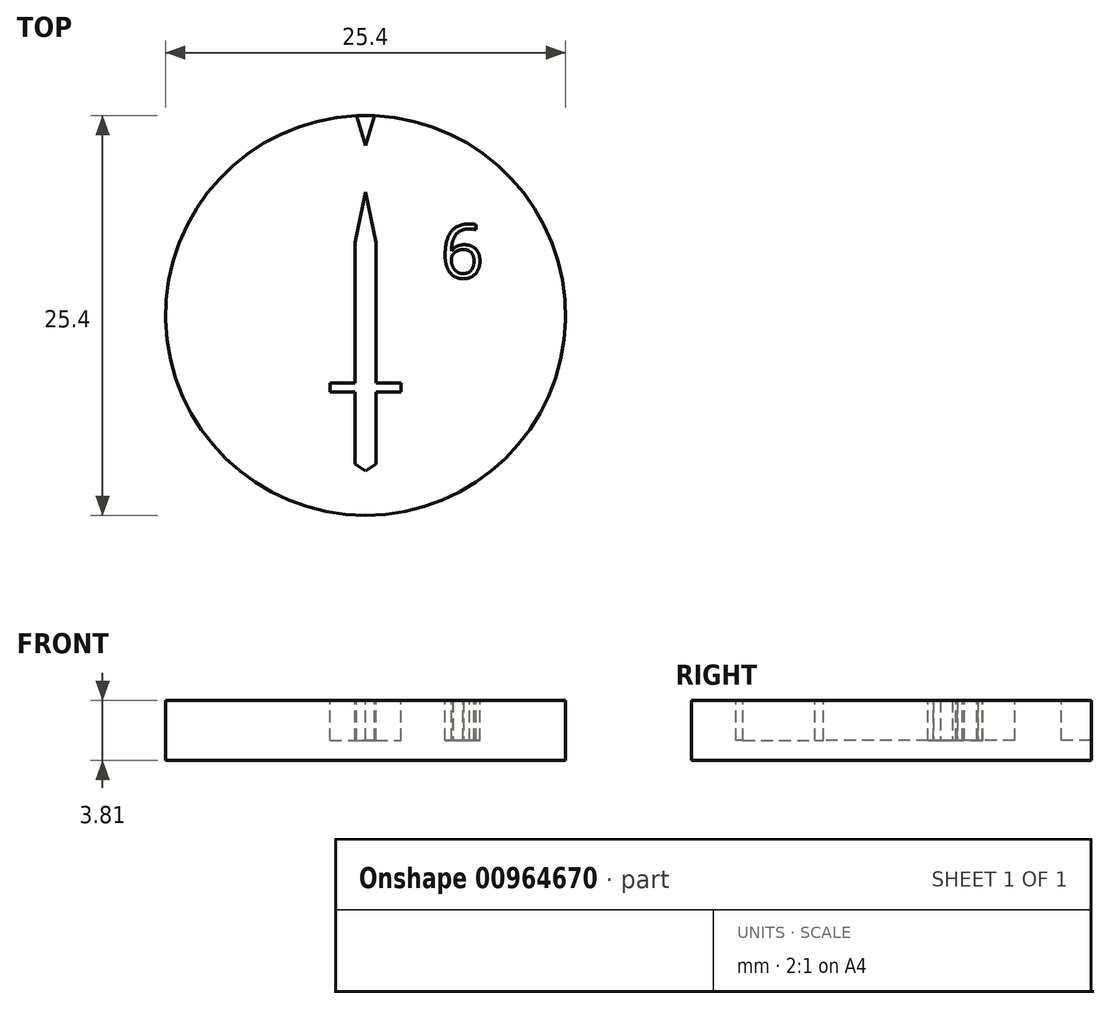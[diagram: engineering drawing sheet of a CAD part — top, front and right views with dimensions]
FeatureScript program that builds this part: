
annotation { "Feature Type Name" : "Feature", "Feature Type Description" : "" }
export const myFeature = defineFeature(function(context is Context, id is Id, definition is map)
    precondition{}
    {
        {
            var Q0;
            Q0=qCreatedBy(makeId("Top.planeOp"),FACE);
            var sketch = newSketch(context, id + "F0", { "sketchPlane" : qUnion([Q0])});
            skCircle(sketch, "E0", {"center": v(0, 0) * mm, "radius": 12.7 * mm});
            skSolve(sketch);
        }
        {
            var Q0;
            Q0=makeQuery(id+"F0.imprint","IMPRINT",FACE,{"disambiguationData":[TD([[makeQuery(id+"F0.imprint","IMPRINT",EDGE,{"derivedFrom":sQuery(id+"F0.wireOp",EDGE,"E0")}),1.0]])]});
            extrude(context, id + "F1", {"entities" : qUnion([Q0]), "depth" : 3.8 * mm, "offsetDistance" : 25.4 * mm});
        }
        {
            var Q0;
            Q0=makeQuery(id+"F1.opExtrude","CAP_FACE",FACE,{"disambiguationData":[OSD([sQuery(id+"F0.wireOp",EDGE,"E0")])],"isStart":false});
            var sketch = newSketch(context, id + "F2", { "sketchPlane" : qUnion([Q0])});
            skLineSegment(sketch, "E1", {"start": v(-0.56, 12.69) * mm, "end": v(0, 10.8) * mm});
            skLineSegment(sketch, "E2", {"start": v(0, 10.8) * mm, "end": v(0.56, 12.69) * mm});
            skLineSegment(sketch, "E3", {"start": v(2.27, -4.3) * mm, "end": v(0.66, -4.3) * mm});
            skLineSegment(sketch, "E4", {"start": v(2.27, -4.3) * mm, "end": v(2.27, -4.86) * mm});
            skLineSegment(sketch, "E5", {"start": v(0.66, -4.86) * mm, "end": v(2.27, -4.86) * mm});
            skLineSegment(sketch, "E6", {"start": v(0.66, -4.86) * mm, "end": v(0.66, -9.43) * mm});
            skLineSegment(sketch, "E7", {"start": v(-0.66, -9.43) * mm, "end": v(-0.66, -4.86) * mm});
            skLineSegment(sketch, "E8", {"start": v(-2.27, -4.86) * mm, "end": v(-0.66, -4.86) * mm});
            skLineSegment(sketch, "E9", {"start": v(-2.27, -4.86) * mm, "end": v(-2.27, -4.3) * mm});
            skLineSegment(sketch, "E10", {"start": v(-0.66, -4.3) * mm, "end": v(-2.27, -4.3) * mm});
            skLineSegment(sketch, "E11", {"start": v(-0.66, -4.3) * mm, "end": v(-0.66, 4.63) * mm});
            skLineSegment(sketch, "E12", {"start": v(-0.66, 4.63) * mm, "end": v(0, 7.84) * mm});
            skLineSegment(sketch, "E13", {"start": v(0, 7.84) * mm, "end": v(0.66, 4.63) * mm});
            skLineSegment(sketch, "E14", {"start": v(0.66, 4.63) * mm, "end": v(0.66, -4.3) * mm});
            skLineSegment(sketch, "E15", {"start": v(-0.66, -9.43) * mm, "end": v(0, -9.88) * mm});
            skLineSegment(sketch, "E16", {"start": v(0, -9.88) * mm, "end": v(0.66, -9.43) * mm});
            skText(sketch, "E17", { "text": "6", "fontName": "OpenSans-Regular.ttf"});
            const initialGuessF2  = {"E17": [0.00478, 0.00238, 1, 0, 0.00342]};
            skSetInitialGuess(sketch, initialGuessF2);
            skSolve(sketch);
        }
        {
            var Q0;
            Q0 = qSketchRegion(id + "F2", true);
            var Q1;
            {var subQ0=sQuery(id+"F2.wireOp",EDGE,"E1");Q1=makeQuery(id+"F2.imprint","IMPRINT",FACE,{"disambiguationData":[TD([[makeQuery(id+"F2.imprint","IMPRINT",EDGE,{"derivedFrom":subQ0}),1.0]])]});}
            extrude(context, id + "F3", {"entities" : qUnion([Q0, Q1]), "operationType" : NewBodyOperationType.REMOVE, "oppositeDirection" : true, "depth" : 2.54 * mm, "offsetDistance" : 25.4 * mm});
        }
    });
